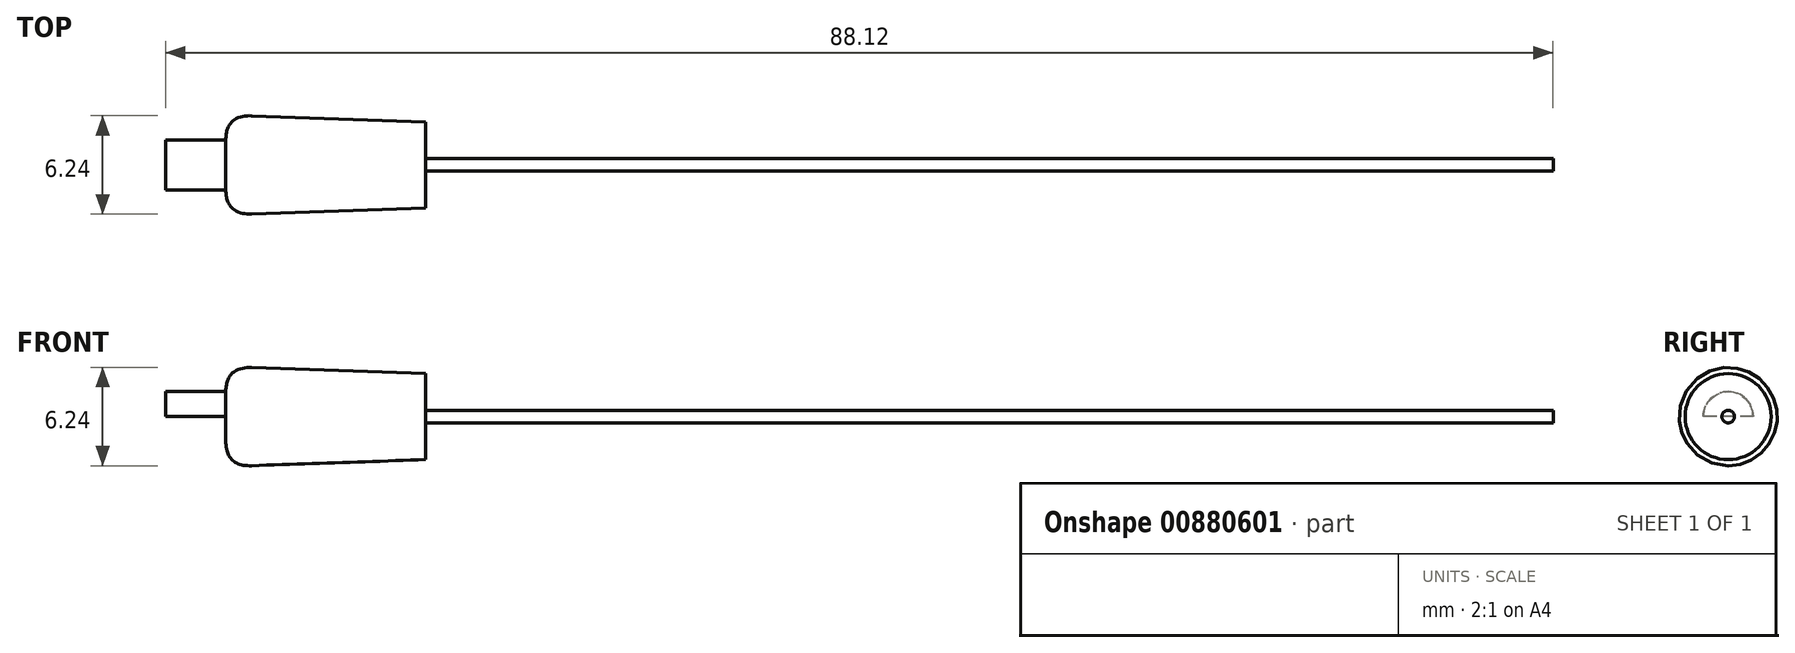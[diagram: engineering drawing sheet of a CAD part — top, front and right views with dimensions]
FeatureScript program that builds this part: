
annotation { "Feature Type Name" : "Feature", "Feature Type Description" : "" }
export const myFeature = defineFeature(function(context is Context, id is Id, definition is map)
    precondition{}
    {
        {
            var Q0;
            Q0=qCreatedBy(makeId("Top.planeOp"),FACE);
            var sketch = newSketch(context, id + "F0", { "sketchPlane" : qUnion([Q0])});
            skLineSegment(sketch, "E0.bottom", {"start": v(1.9, 1.59) * mm, "end": v(-1.9, 1.59) * mm});
            skLineSegment(sketch, "E0.top", {"start": v(1.9, -1.59) * mm, "end": v(-1.9, -1.59) * mm});
            skLineSegment(sketch, "E0.left", {"start": v(1.9, -1.59) * mm, "end": v(1.9, 1.59) * mm});
            skLineSegment(sketch, "E0.right", {"start": v(-1.9, -1.59) * mm, "end": v(-1.9, 1.59) * mm});
            skPoint(sketch, "E0.middle", {"position": v(0, 0) * mm});
            skLineSegment(sketch, "E1", {"start": v(-1.9, 0) * mm, "end": v(1.9, 0) * mm});
            skSolve(sketch);
        }
        {
            var Q0;
            {var subQ0=sQuery(id+"F0.wireOp",EDGE,"E0.bottom");Q0=makeQuery(id+"F0.imprint","IMPRINT",FACE,{"disambiguationData":[TD([[makeQuery(id+"F0.imprint","IMPRINT",EDGE,{"derivedFrom":subQ0}),1.0]])]});}
            var Q1;
            Q1=sQuery(id+"F0.wireOp",EDGE,"E1");
            revolve(context, id + "F1", {"surfaceOperationType" : NewSurfaceOperationType.NEW, "entities" : qUnion([Q0]), "axis" : qUnion([Q1]), "revolveType" : RevolveType.ONE_DIRECTION, "angle" : 180 * degree});
        }
        {
            var Q0;
            Q0=makeQuery(id+"F1.opRevolve","SWEPT_FACE",FACE,{"disambiguationData":[OSD([sQuery(id+"F0.wireOp",EDGE,"E0.left")])]});
            var sketch = newSketch(context, id + "F2", { "sketchPlane" : qUnion([Q0])});
            skCircle(sketch, "E2", {"center": v(0, 0) * mm, "radius": 3.18 * mm});
            skSolve(sketch);
        }
        {
            var Q0;
            Q0=makeQuery(id+"F2.imprint","IMPRINT",FACE,{"disambiguationData":[TD([[makeQuery(id+"F2.imprint","IMPRINT",EDGE,{"derivedFrom":sQuery(id+"F2.wireOp",EDGE,"E2")}),1.0]])]});
            var Q1;
            {var subQ0=sQuery(id+"F0.wireOp",EDGE,"E0.left");Q1=makeQuery(id+"F2.imprint","IMPRINT",FACE,{"disambiguationData":[TD([[makeQuery(id+"F2.imprint","IMPRINT",EDGE,{"derivedFrom":makeQuery(id+"F1.opRevolve","CAP_EDGE",EDGE,{"disambiguationData":[OSD([subQ0])],"isStart":false})}),-1.0]])]});}
            extrude(context, id + "F3", {"entities" : qUnion([Q0, Q1]), "operationType" : NewBodyOperationType.ADD, "depth" : 12.7 * mm, "offsetDistance" : 25.4 * mm, "hasDraft" : true, "draftAngle" : 2 * degree, "draftPullDirection" : true});
        }
        {
            var Q0;
            Q0=makeQuery(id+"F3.opExtrude","CAP_EDGE",EDGE,{"disambiguationData":[OSD([sQuery(id+"F2.wireOp",EDGE,"E2")])],"isStart":true});
            fillet(context, id + "F4", {"entities" : qUnion([Q0]), "radius" : 1.59 * mm, "tangentPropagation" : true, "rho" : 0.5, "crossSection" : FilletCrossSection.CONIC, "allowEdgeOverflow" : false});
        }
        {
            var Q0;
            Q0=qCreatedBy(makeId("Front.planeOp"),FACE);
            var sketch = newSketch(context, id + "F5", { "sketchPlane" : qUnion([Q0])});
            skFitSpline(sketch, "E3", {"points": [v(14.62, 0) * mm, v(86.23, 0) * mm], "startDerivative": vector(71.6, 0) * mm, "endDerivative": vector(71.6, 0) * mm});
            skSolve(sketch);
        }
        {
            var Q0;
            Q0=makeQuery(id+"F3.opExtrude","CAP_FACE",FACE,{"disambiguationData":[OSD([sQuery(id+"F2.wireOp",EDGE,"E2")])],"isStart":false});
            var sketch = newSketch(context, id + "F6", { "sketchPlane" : qUnion([Q0])});
            skCircle(sketch, "E4", {"center": v(0, 0) * mm, "radius": 0.4 * mm});
            skSolve(sketch);
        }
        {
            var Q0;
            Q0=makeQuery(id+"F6.imprint","IMPRINT",FACE,{"disambiguationData":[TD([[makeQuery(id+"F6.imprint","IMPRINT",EDGE,{"derivedFrom":sQuery(id+"F6.wireOp",EDGE,"E4")}),1.0]])]});
            var Q1;
            Q1=sQuery(id+"F5.wireOp",EDGE,"E3");
            sweep(context, id + "F7", {"operationType" : NewBodyOperationType.ADD, "profiles" : qUnion([Q0]), "path" : qUnion([Q1])});
        }
    });
